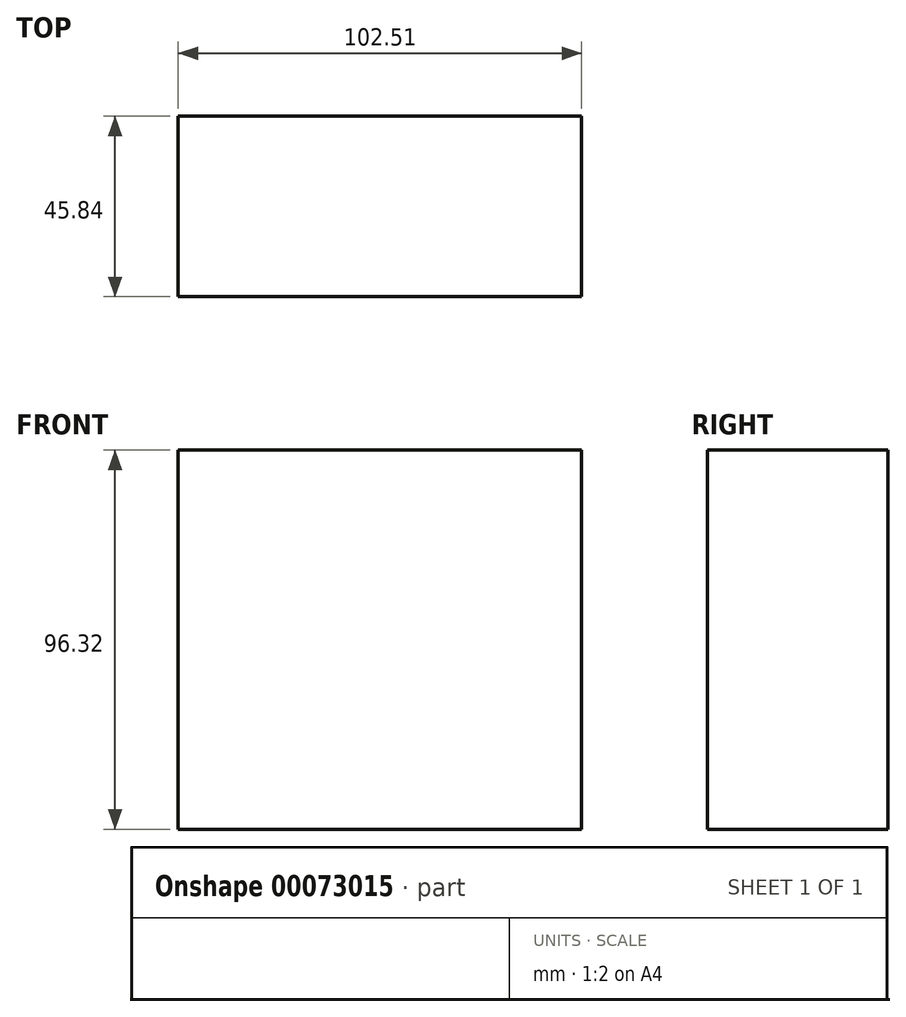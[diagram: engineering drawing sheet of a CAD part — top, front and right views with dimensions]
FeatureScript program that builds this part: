
annotation { "Feature Type Name" : "Feature", "Feature Type Description" : "" }
export const myFeature = defineFeature(function(context is Context, id is Id, definition is map)
    precondition{}
    {
        {
            var Q0;
            Q0=qCreatedBy(makeId("Front.planeOp"),FACE);
            var sketch = newSketch(context, id + "F0", { "sketchPlane" : qUnion([Q0])});
            skLineSegment(sketch, "E0", {"start": v(-47.72, 46.17) * mm, "end": v(-47.72, -50.15) * mm});
            skLineSegment(sketch, "E1", {"start": v(-47.72, -50.15) * mm, "end": v(54.8, -50.15) * mm});
            skLineSegment(sketch, "E2", {"start": v(54.8, -50.15) * mm, "end": v(54.8, 46.17) * mm});
            skLineSegment(sketch, "E3", {"start": v(54.8, 46.17) * mm, "end": v(-47.72, 46.17) * mm});
            skSolve(sketch);
        }
        {
            var Q0;
            Q0=makeQuery(id+"F0.imprint","IMPRINT",FACE,{"disambiguationData":[TD([[makeQuery(id+"F0.imprint","IMPRINT",EDGE,{"derivedFrom":sQuery(id+"F0.wireOp",EDGE,"E0")}),1.0]])]});
            extrude(context, id + "F1", {"entities" : qUnion([Q0]), "depth" : 45.84 * mm});
        }
    });
